# Revit family: IS_Alu+_BD581_BIM_NL
name_source: partatom
category: Plumbing Fixtures
units: mm (PartAtom-declared; Revit-internal decimal feet)

## family parameters
Always vertical = No
Cut with Voids When Loaded = No
OmniClass Number = 23.45.05.14.17
OmniClass Title = Showers
Part Type = Normal
Room Calculation Point = No
Round Connector Dimension = Use Diameter
Shared = No
Work Plane-Based = No

## types (3) — shared parameters
Accesoires = https://www.idealstandard.nl
Accessories = https://www.idealstandard.nl
Afmetingen = 260 x 260 x 87 mm
AfstandsEenheid = Millimeter
AreaUnits = millimeters
AssetType = Fixed
Auteur = IdealStandard
BIMObjectName = ISI_IdealStandard_Shower mixers_Alu+_BD581
BIMobject category = Showers
BIMobject category code = showers
BIMobject main category = Sanitary
BIMobject main category code = sanitary
Beschrijvinggarantie = Herstellergarantie
BimObjectNaam = ISI_IdealStandard_Shower mixers_Alu+_BD581
Brand = Ideal Standard
Brand url = https://www.idealstandard.nl
Breedte = 259.943527
ConnectionType = Plumbing
CurrencyUnit = €
CurrentRevision = 1
Date of publishing = 01/06/2023
Debiet = 12l/min
Design country = Italy
DurationUnit = Year
Edition number = 1
Garantieonderdelen = 5
Garantieunits = Jaren
GemaaktOp = 01/06/2023
Help = https://www.idealstandard.nl
Hoogte = 86,7422979892879
Hulp = https://www.idealstandard.nl
IFC Classification = Sanitary Terminal
IfcExportAs = IfcValveType
IfcExportType = FAUCET
Installatieinstructies = https://www.idealstandard.nl
Installation instructions = https://www.idealstandard.nl
InstallationInstructions = https://www.idealstandard.nl
Lengte = 260 mm
LinearUnits = millimeters
MaintenanceInformation = https://www.idealstandard.nl
Manufacturer = Ideal Standard
Manufacturer name = Ideal Standard
ManufacturerURL = https://www.idealstandard.nl
Materiaal = Messing
Material = Brass
Material main = Brass
Merk = Ideal Standard
NBS Reference Code = 45-35-70/315
NBS Reference Description = Shower mixers
Name = Shower mixers_Alu+_BD581_IdealStandard
NettWeight = 1,29
NominalDepth = 260 mm
NominalHeight = 87 mm
NominalLength = 260 mm
NominalWidth = 260 mm
OmniClass Code = 23-31 11 00
OmniClass Description = Faucets
OppervlakteEenheid = Millimeter
Product Guid = c43d4811-3084-4c01-9a11-edc3e384d5fc
Product SKU = BD581
Product certification = https://www.idealstandard.nl
Product data url = https://bimobject.com
Product family = Alu+
Product group = Alu+
Product name = IR ALU+ SHOWER HEAD RND 2F 260MM RO
Product url = https://www.idealstandard.nl
ProductInformation = https://www.idealstandard.nl
ProductSoort = Sanitary
Productinformatie = https://www.idealstandard.nl
QR code = http://bimobject.com
Revisie = 1
Shape = Cylindrical
Size = 260 x 260 x 87 mm
Space = Internal
SpareParts = https://www.idealstandard.nl
Technical description = https://www.idealstandard.nl
Telefoonnummer = 077 355 08 08
TestPressure = 10 bar
Typeconnectie = Installation
UNSPSC Code = 30181700
URL = https://www.idealstandard.nl
Uniclass 1.4 Code = L725111
Uniclass 1.4 Description = Mixer taps
Uniclass 2.0 Code = Pr_40_30_96_81
Uniclass 2.0 Description = Shower Thermostatic Water Supply Sets
Uniclass 2015 Code = Pr_40_20_87_78
Uniclass 2015 Name = Shower manual water supply sets
Uniclass2015Beschrijving = Pr_40_20_87_78
Uniclass2015Code = Pr_40_20_87_78
Uniclass2015Referentie = Pr_40_20_87_78
Uniclass2015Title = Shower manual water supply sets
Uniclass2015Version = v1.20
Urlproducent = https://www.idealstandard.nl
ValutaEenheid = €
Version = 1
VolumeUnits = Litres
Volumeunits = Liters
Vorm = zylindrisch
WRASURL = https://www.wrasapprovals.co.uk
WarrantyDescription = Manufacturers Warranty
WarrantyDurationParts = 5
WarrantyDurationUnit = Year
WarrantyGuarantorParts = https://www.idealstandard.nl
Weight Net (Kg) = 1.29
Youtube clip = https://www.youtube.com
zero-valued in all types: BrutoGewicht, Default Elevation, Diepte, Nettogewicht, Vervangingskosten

## per-type parameters (varying)
| type | Afwerking | Artikelnummer | Artikelomschrijving | Artikelreferentie | BarCode | Barcode | Color | Description | Features | Finish | GTIN code | Kleur | MainColor | Model | ModelNumber |
| BD581RO - IR ALU+ SHOWER HEAD RND 2F 260MM RO | Roos | BD581RO | IR ALU+ SHOWER HEAD RND 2F 260MM RO | IR ALU+ SHOWER HEAD RND 2F 260MM RO | 3800861117384 | 3800861117384 | Rose | IR Alu+ Douchekop, 2 functies, 260MM, 2 sproeimodi (regen, zijdezacht), water- en energiebesparing, eenvoudig schoon te maken, zwarte sproeisurface en nozzles, eenvoudige bediening voor het wisselen van sproeimodi door rotatie van de knop in het midden, rosé. | IR Alu+ Douchekop, 2 functies, 260MM, 2 sproeimodi (regen, zijdezacht), water- en energiebesparing, eenvoudig schoon te maken, zwarte sproeisurface en nozzles, eenvoudige bediening voor het wisselen van sproeimodi door rotatie van de knop in het midden, rosé. | Rose | 3800861117384 | Roos | Rose | BD581RO | BD581RO |
| BD581SI - IR ALU+ SHOWER HEAD RND 2F 260MM SI | Zilver | BD581SI | IR ALU+ SHOWER HEAD RND 2F 260MM SI | IR ALU+ SHOWER HEAD RND 2F 260MM SI | 3800861117261 | 3800861117261 | Silver | IR Alu+ Douchekop, 2 functies, 260MM, 2 sproeimodi (regen, zijdezacht), water- en energiebesparing, eenvoudig schoon te maken, zilveren sproeisurface en nozzles, eenvoudige bediening voor het wisselen van sproeimodi door rotatie van de knop in het midden. | IR Alu+ Douchekop, 2 functies, 260MM, 2 sproeimodi (regen, zijdezacht), water- en energiebesparing, eenvoudig schoon te maken, zilveren sproeisurface en nozzles, eenvoudige bediening voor het wisselen van sproeimodi door rotatie van de knop in het midden. | Silver | 3800861117261 | Zilver | Silver | BD581SI | BD581SI |
| BD581XG - IR ALU+ SHOWER HEAD RND 2F 260MM XG | Zijde Zwart | BD581XG | IR ALU+ SHOWER HEAD RND 2F 260MM XG | IR ALU+ SHOWER HEAD RND 2F 260MM XG | 3800861117148 | 3800861117148 | Silk Black | IR ALU+ DOUCHEKOP, 2 functies, 260MM, 2 sproeimodi (regen, zijdezacht), water- en energiebesparing, eenvoudig schoon te maken, zwarte sproeisurface en nozzles, eenvoudige bediening voor het wisselen van sproeimodi door rotatie van de knop in het midden, zijdezwart. | IR ALU+ DOUCHEKOP, 2 functies, 260MM, 2 sproeimodi (regen, zijdezacht), water- en energiebesparing, eenvoudig schoon te maken, zwarte sproeisurface en nozzles, eenvoudige bediening voor het wisselen van sproeimodi door rotatie van de knop in het midden, zijdezwart. | Silk Black | 3800861117148 | Zijde Zwart | Silk Black | BD581XG | BD581XG |

note: column(s) folded — value = type name in every type: Eigenschappen, ModelReference, Referentie

## geometry (parser evidence)
native form markers: Blend x4, Sweep x4
no freeform markers — native parametric forms only
